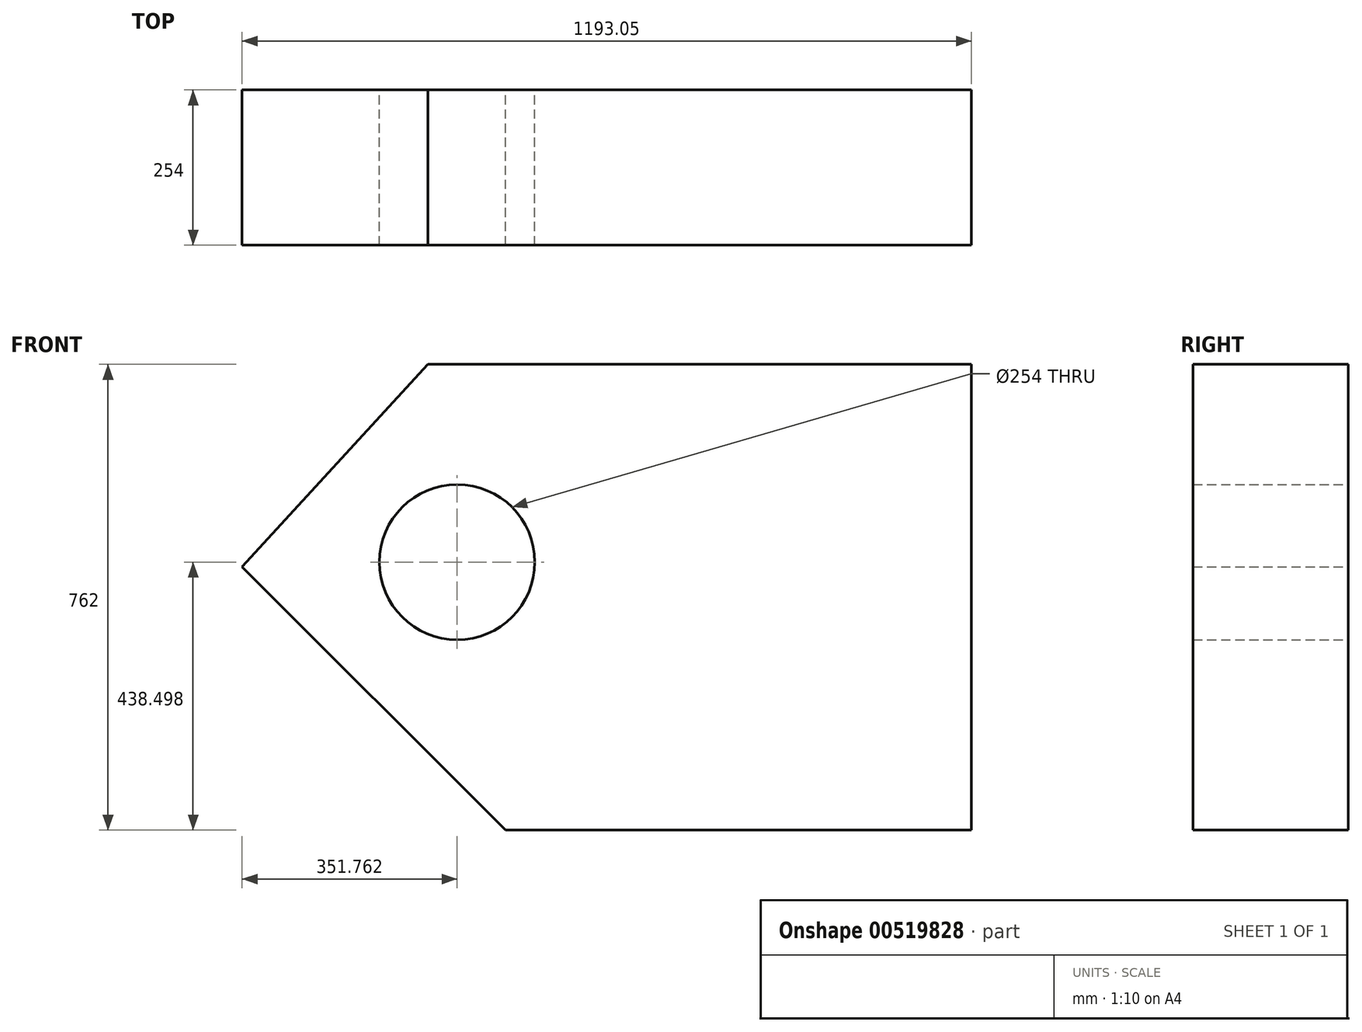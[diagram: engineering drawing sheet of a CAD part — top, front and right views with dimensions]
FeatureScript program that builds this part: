
annotation { "Feature Type Name" : "Feature", "Feature Type Description" : "" }
export const myFeature = defineFeature(function(context is Context, id is Id, definition is map)
    precondition{}
    {
        {
            var Q0;
            Q0=qCreatedBy(makeId("Front.planeOp"),FACE);
            var sketch = newSketch(context, id + "F0", { "sketchPlane" : qUnion([Q0])});
            skLineSegment(sketch, "E0", {"start": v(762, 0) * mm, "end": v(762, 762) * mm});
            skLineSegment(sketch, "E1", {"start": v(762, 762) * mm, "end": v(-127, 762) * mm});
            skLineSegment(sketch, "E2", {"start": v(-127, 762) * mm, "end": v(-431.05, 431.05) * mm});
            skLineSegment(sketch, "E3", {"start": v(-431.05, 431.05) * mm, "end": v(0, 0) * mm});
            skCircle(sketch, "E4", {"center": v(-79.29, 438.5) * mm, "radius": 127 * mm});
            skLineSegment(sketch, "E5", {"start": v(0, 0) * mm, "end": v(762, 0) * mm});
            skSolve(sketch);
        }
        {
            var Q0;
            Q0 = qSketchRegion(id + "F0", true);
            extrude(context, id + "F1", {"entities" : qUnion([Q0]), "depth" : 254 * mm, "offsetDistance" : 25.4 * mm});
        }
    });
